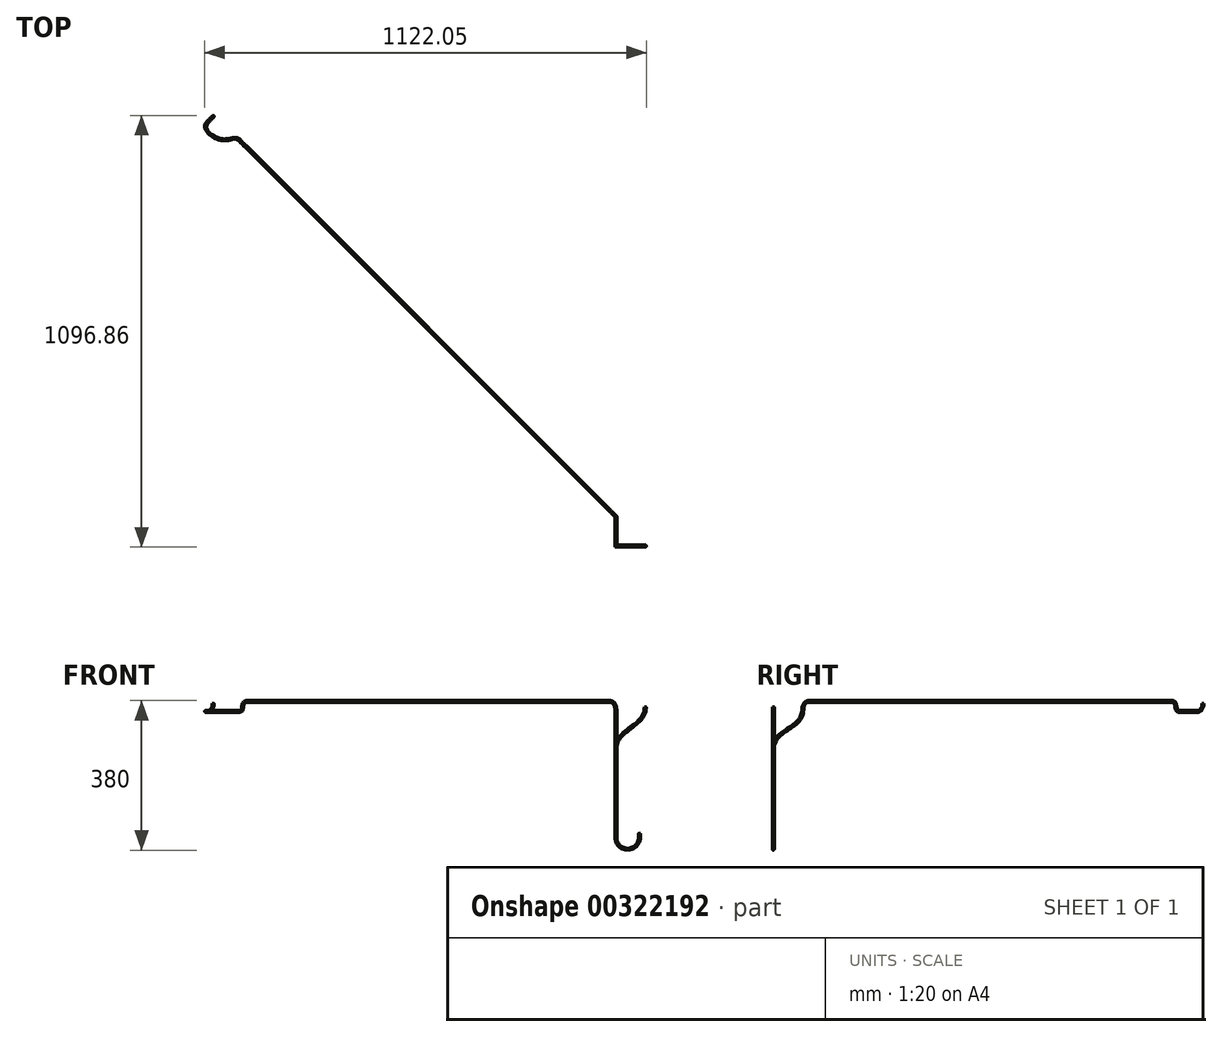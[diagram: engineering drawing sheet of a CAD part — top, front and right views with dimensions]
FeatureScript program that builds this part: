
annotation { "Feature Type Name" : "Feature", "Feature Type Description" : "" }
export const myFeature = defineFeature(function(context is Context, id is Id, definition is map)
    precondition{}
    {
        {
            var Q0;
            Q0=qCreatedBy(makeId("Top.planeOp"),FACE);
            var sketch = newSketch(context, id + "F0", { "sketchPlane" : qUnion([Q0])});
            skCircle(sketch, "E0", {"center": v(0, 0) * mm, "radius": 2.5 * mm});
            skSolve(sketch);
        }
        {
            var Q0;
            Q0=qCreatedBy(makeId("Front.planeOp"),FACE);
            var sketch = newSketch(context, id + "F1", { "sketchPlane" : qUnion([Q0])});
            skLineSegment(sketch, "E1", {"start": v(0, 0) * mm, "end": v(0, -10) * mm});
            skArc(sketch, "E2", {"start": v(-60, -10) * mm, "mid": v(-30, -40) * mm, "end": v(0, -10) * mm});
            skLineSegment(sketch, "E3", {"start": v(-60, -10) * mm, "end": v(-60, 215) * mm});
            skFitSpline(sketch, "E4", {"points": [v(-60, 215) * mm, v(-22.5, 268) * mm, v(15, 321) * mm], "startDerivative": vector(0, 150) * mm, "endDerivative": vector(0, 150) * mm});
            skLineSegment(sketch, "E5", {"start": v(15, 296) * mm, "end": v(15, 321) * mm, "construction": true});
            skLineSegment(sketch, "E6", {"start": v(-60, 240) * mm, "end": v(-60, 215) * mm, "construction": true});
            skLineSegment(sketch, "E7", {"start": v(15, 321) * mm, "end": v(-60, 215) * mm, "construction": true});
            skSolve(sketch);
        }
        {
            var Q0;
            Q0=qSketchRegion(id+"F0",true);
            var Q1;
            Q1=qConstructionFilter(qBodyType(qCreatedBy(id+"F1",EDGE),BodyType.WIRE),ConstructionObject.NO);
            sweep(context, id + "F2", {"profiles" : qUnion([Q0]), "path" : qUnion([Q1])});
        }
        {
            var Q0;
            Q0=qCreatedBy(makeId("Front.planeOp"),FACE);
            var sketch = newSketch(context, id + "F3", { "sketchPlane" : qUnion([Q0])});
            skLineSegment(sketch, "E8", {"start": v(0, 0) * mm, "end": v(0, -10) * mm});
            skArc(sketch, "E9", {"start": v(-60, -10) * mm, "mid": v(-30, -40) * mm, "end": v(0, -10) * mm});
            skLineSegment(sketch, "E10", {"start": v(-60, -10) * mm, "end": v(-60, 215) * mm});
            skSolve(sketch);
        }
        {
            var Q0;
            Q0=qCreatedBy(makeId("Right.planeOp"),FACE);
            var Q1;
            Q1=sQuery(id+"F3.wireOp",VERTEX,"E10.end");
            cPlane(context, id + "F4", {"entities" : qUnion([Q0, Q1]), "cplaneType" : CPlaneType.PLANE_POINT, "offset" : 25 * mm, "width" : 150 * mm, "height" : 150 * mm});
        }
        {
            var Q0;
            Q0=qCreatedBy(id+"F4.planeOp",FACE);
            var sketch = newSketch(context, id + "F5", { "sketchPlane" : qUnion([Q0])});
            skFitSpline(sketch, "E11", {"points": [v(0, 215) * mm, v(37.5, 265) * mm, v(75, 315) * mm], "startDerivative": vector(0, 150) * mm, "endDerivative": vector(0, 150) * mm});
            skLineSegment(sketch, "E12", {"start": v(75, 290) * mm, "end": v(75, 315) * mm, "construction": true});
            skLineSegment(sketch, "E13", {"start": v(0, 240) * mm, "end": v(0, 215) * mm, "construction": true});
            skLineSegment(sketch, "E14", {"start": v(0, 215) * mm, "end": v(75, 315) * mm, "construction": true});
            skSolve(sketch);
        }
        {
            var Q0;
            Q0=sQuery(id+"F5.wireOp",EDGE,"E12");
            cPlane(context, id + "F6", {"entities" : qUnion([Q0]), "cplaneType" : CPlaneType.LINE_ANGLE, "offset" : 25 * mm, "angle" : 135 * degree, "oppositeDirection" : true, "width" : 150 * mm, "height" : 150 * mm});
        }
        {
            var Q0;
            Q0=qCreatedBy(id+"F6.planeOp",FACE);
            var sketch = newSketch(context, id + "F7", { "sketchPlane" : qUnion([Q0])});
            skArc(sketch, "E15", {"start": v(-95.46, 315) * mm, "mid": v(-101.32, 329.14) * mm, "end": v(-115.46, 335) * mm});
            skLineSegment(sketch, "E16", {"start": v(-115.46, 335) * mm, "end": v(-1423.46, 335) * mm});
            skFitSpline(sketch, "E17", {"points": [v(-1423.46, 335) * mm, v(-1435.96, 322.5) * mm, v(-1448.46, 310) * mm], "startDerivative": vector(-60, 0) * mm, "endDerivative": vector(-60, 0) * mm});
            skLineSegment(sketch, "E18", {"start": v(-1433.46, 335) * mm, "end": v(-1423.46, 335) * mm, "construction": true});
            skLineSegment(sketch, "E19", {"start": v(-1438.46, 310) * mm, "end": v(-1448.46, 310) * mm, "construction": true});
            skLineSegment(sketch, "E20", {"start": v(-1448.46, 310) * mm, "end": v(-1423.46, 335) * mm, "construction": true});
            skSolve(sketch);
        }
        {
            var Q0;
            Q0=sQuery(id+"F7.wireOp",EDGE,"E19");
            cPlane(context, id + "F8", {"entities" : qUnion([Q0]), "cplaneType" : CPlaneType.LINE_ANGLE, "offset" : 25 * mm, "angle" : 0 * degree, "width" : 150 * mm, "height" : 150 * mm});
        }
        {
            var Q0;
            Q0=qCreatedBy(id+"F8.planeOp",FACE);
            var sketch = newSketch(context, id + "F9", { "sketchPlane" : qUnion([Q0])});
            skFitSpline(sketch, "E21", {"points": [v(-1016.72, 1031.72) * mm, v(-1061.72, 1032.72) * mm, v(-1096.72, 1077.72) * mm], "startDerivative": vector(-67.63, 67.63) * mm, "endDerivative": vector(100.16, 100.16) * mm});
            skLineSegment(sketch, "E22", {"start": v(-1114.4, 1060.04) * mm, "end": v(-1096.72, 1077.72) * mm, "construction": true});
            skLineSegment(sketch, "E23", {"start": v(-1016.72, 1031.72) * mm, "end": v(-1027.32, 1042.32) * mm, "construction": true});
            skSolve(sketch);
        }
        {
            var Q0;
            Q0=sQuery(id+"F9.wireOp",EDGE,"E22");
            cPlane(context, id + "F10", {"entities" : qUnion([Q0]), "cplaneType" : CPlaneType.LINE_ANGLE, "offset" : 25 * mm, "angle" : 90 * degree, "width" : 150 * mm, "height" : 150 * mm});
        }
        {
            var Q0;
            Q0=qCreatedBy(id+"F10.planeOp",FACE);
            var sketch = newSketch(context, id + "F11", { "sketchPlane" : qUnion([Q0])});
            skArc(sketch, "E24", {"start": v(-13.44, 310) * mm, "mid": v(0.7, 315.86) * mm, "end": v(6.56, 330) * mm});
            skSolve(sketch);
        }
        {
            var Q0;
            Q0=qSketchRegion(id+"F0",true);
            var Q1;
            Q1=qConstructionFilter(qBodyType(qCreatedBy(id+"F3",EDGE),BodyType.WIRE),ConstructionObject.NO);
            var Q2;
            Q2=qConstructionFilter(qBodyType(qCreatedBy(id+"F5",EDGE),BodyType.WIRE),ConstructionObject.NO);
            var Q3;
            Q3=qConstructionFilter(qBodyType(qCreatedBy(id+"F7",EDGE),BodyType.WIRE),ConstructionObject.NO);
            var Q4;
            Q4=qConstructionFilter(qBodyType(qCreatedBy(id+"F9",EDGE),BodyType.WIRE),ConstructionObject.NO);
            var Q5;
            Q5=qConstructionFilter(qBodyType(qCreatedBy(id+"F11",EDGE),BodyType.WIRE),ConstructionObject.NO);
            sweep(context, id + "F12", {"profiles" : qUnion([Q0]), "path" : qUnion([Q1, Q2, Q3, Q4, Q5])});
        }
    });
